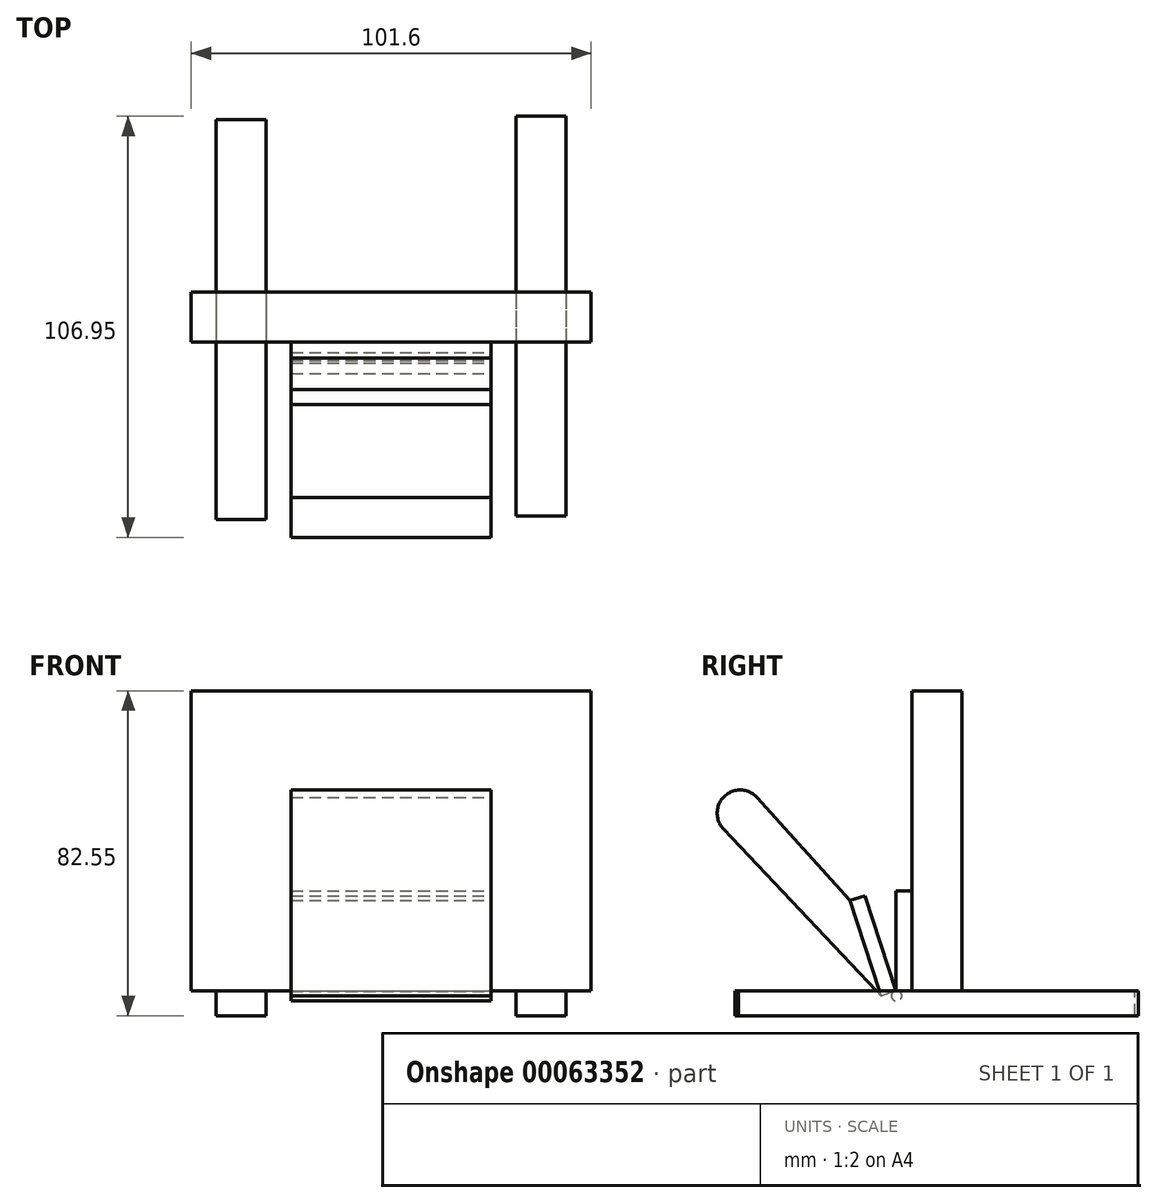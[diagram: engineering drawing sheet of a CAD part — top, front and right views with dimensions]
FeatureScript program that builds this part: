
annotation { "Feature Type Name" : "Feature", "Feature Type Description" : "" }
export const myFeature = defineFeature(function(context is Context, id is Id, definition is map)
    precondition{}
    {
        {
            var Q0;
            Q0=qCreatedBy(makeId("Front.planeOp"),FACE);
            var sketch = newSketch(context, id + "F0", { "sketchPlane" : qUnion([Q0])});
            skLineSegment(sketch, "E0.bottom", {"start": v(0, 0) * mm, "end": v(101.6, 0) * mm});
            skLineSegment(sketch, "E0.top", {"start": v(0, 76.2) * mm, "end": v(101.6, 76.2) * mm});
            skLineSegment(sketch, "E0.left", {"start": v(0, 0) * mm, "end": v(0, 76.2) * mm});
            skLineSegment(sketch, "E0.right", {"start": v(101.6, 0) * mm, "end": v(101.6, 76.2) * mm});
            skSolve(sketch);
        }
        {
            var Q0;
            Q0 = qSketchRegion(id + "F0", true);
            extrude(context, id + "F1", {"entities" : qUnion([Q0]), "depth" : 12.7 * mm});
        }
        {
            var Q0;
            Q0=makeQuery(id+"F1.opExtrude","CAP_FACE",FACE,{"disambiguationData":[OSD([sQuery(id+"F0.wireOp",EDGE,"E0.bottom"),sQuery(id+"F0.wireOp",EDGE,"E0.top"),sQuery(id+"F0.wireOp",EDGE,"E0.left"),sQuery(id+"F0.wireOp",EDGE,"E0.right")])],"isStart":false});
            var sketch = newSketch(context, id + "F2", { "sketchPlane" : qUnion([Q0])});
            skLineSegment(sketch, "E1.rect.bottom", {"start": v(25.4, 0) * mm, "end": v(76.2, 0) * mm});
            skLineSegment(sketch, "E1.rect.top", {"start": v(25.4, 25.4) * mm, "end": v(76.2, 25.4) * mm});
            skLineSegment(sketch, "E1.rect.left", {"start": v(25.4, 0) * mm, "end": v(25.4, 25.4) * mm});
            skLineSegment(sketch, "E1.rect.right", {"start": v(76.2, 0) * mm, "end": v(76.2, 25.4) * mm});
            skPoint(sketch, "E1.rect.middle", {"position": v(50.8, 12.7) * mm});
            skPoint(sketch, "E1.rect.middle.positionSnap0", {"position": v(50.8, 0) * mm});
            skPoint(sketch, "E1.rect.centerSnap0", {"position": v(50.8, 0) * mm});
            skSolve(sketch);
        }
        {
            var Q0;
            Q0 = qSketchRegion(id + "F2", true);
            extrude(context, id + "F3", {"entities" : qUnion([Q0]), "operationType" : NewBodyOperationType.ADD, "depth" : 4.06 * mm});
        }
        {
            var Q0;
            Q0=makeQuery(id+"F3.opExtrude","SWEPT_FACE",FACE,{"disambiguationData":[OSD([sQuery(id+"F2.wireOp",EDGE,"E1.rect.right")])]});
            var sketch = newSketch(context, id + "F4", { "sketchPlane" : qUnion([Q0])});
            skLineSegment(sketch, "E2", {"start": v(-16.76, 0) * mm, "end": v(-24.66, 24.14) * mm});
            skLineSegment(sketch, "E3", {"start": v(-24.66, 24.14) * mm, "end": v(-28.52, 22.88) * mm});
            skLineSegment(sketch, "E4", {"start": v(-28.52, 22.88) * mm, "end": v(-20.63, -1.26) * mm});
            skLineSegment(sketch, "E5", {"start": v(-20.63, -1.26) * mm, "end": v(-16.76, 0) * mm});
            skSolve(sketch);
        }
        {
            var Q0;
            Q0=makeQuery(id+"F4.imprint","IMPRINT",FACE,{"disambiguationData":[TD([[makeQuery(id+"F4.imprint","IMPRINT",EDGE,{"derivedFrom":sQuery(id+"F4.wireOp",EDGE,"E2")}),1.0]])]});
            extrude(context, id + "F5", {"entities" : qUnion([Q0]), "oppositeDirection" : true, "depth" : 50.8 * mm});
        }
        {
            var Q0;
            Q0=makeQuery(id+"F3.opExtrude","SWEPT_FACE",FACE,{"disambiguationData":[OSD([sQuery(id+"F2.wireOp",EDGE,"E1.rect.right")])]});
            var sketch = newSketch(context, id + "F6", { "sketchPlane" : qUnion([Q0])});
            skCircle(sketch, "E6", {"center": v(-16.66, -1.31) * mm, "radius": 1.32 * mm});
            skPoint(sketch, "E6.first.point", {"position": v(-16.76, 0) * mm});
            skPoint(sketch, "E6.second.point", {"position": v(-16.34, -2.6) * mm});
            skPoint(sketch, "E6.third.point", {"position": v(-16.76, -2.63) * mm});
            skSolve(sketch);
        }
        {
            var Q0;
            {var subQ0=sQuery(id+"F6.wireOp",EDGE,"E6");var subQ1=sQuery(id+"F2.wireOp",EDGE,"E1.rect.right");var subQ2=makeQuery(id+"F3.opExtrude","SWEPT_EDGE",EDGE,{"disambiguationData":[OSD([sQuery(id+"F0.wireOp",EDGE,"E0.bottom"),sQuery(id+"F2.wireOp",EDGE,"E1.rect.bottom"),subQ1])]});var subQ4=makeQuery(id+"F6.imprint","INTERSECT",VERTEX,{"derivedFrom":[subQ2,subQ0]});Q0=makeQuery(id+"F6.imprint","IMPRINT",FACE,{"disambiguationData":[TD([[makeQuery(id+"F6.imprint","IMPRINT",EDGE,{"disambiguationData":[TD([[subQ4,1.0]])],"derivedFrom":subQ0}),1.0]])]});}
            extrude(context, id + "F7", {"entities" : qUnion([Q0]), "operationType" : NewBodyOperationType.ADD, "oppositeDirection" : true, "depth" : 50.8 * mm});
        }
        {
            var Q0;
            Q0=makeQuery(id+"F7.boolean.opBoolean","MERGE",FACE,{"derivedFrom":[makeQuery(id+"F5.opExtrude","CAP_FACE",FACE,{"disambiguationData":[OSD([sQuery(id+"F4.wireOp",EDGE,"E2"),sQuery(id+"F4.wireOp",EDGE,"E3"),sQuery(id+"F4.wireOp",EDGE,"E4"),sQuery(id+"F4.wireOp",EDGE,"E5")])],"isStart":true}),makeQuery(id+"F7.opExtrude","CAP_FACE",FACE,{"disambiguationData":[OSD([sQuery(id+"F0.wireOp",EDGE,"E0.bottom"),sQuery(id+"F2.wireOp",EDGE,"E1.rect.bottom"),sQuery(id+"F2.wireOp",EDGE,"E1.rect.right"),sQuery(id+"F6.wireOp",EDGE,"E6")])],"isStart":true})]});
            var sketch = newSketch(context, id + "F8", { "sketchPlane" : qUnion([Q0])});
            skLineSegment(sketch, "E7", {"start": v(-28.52, 22.88) * mm, "end": v(-52.1, 49.1) * mm});
            skLineSegment(sketch, "E8", {"start": v(-20.63, -1.26) * mm, "end": v(-60.64, 41.1) * mm});
            skArc(sketch, "E9", {"start": v(-52.1, 49.1) * mm, "mid": v(-60.4, 49.38) * mm, "end": v(-60.64, 41.1) * mm});
            skSolve(sketch);
        }
        {
            var Q0;
            Q0=makeQuery(id+"F8.imprint","IMPRINT",FACE,{"disambiguationData":[TD([[makeQuery(id+"F8.imprint","IMPRINT",EDGE,{"derivedFrom":sQuery(id+"F8.wireOp",EDGE,"E7")}),1.0]])]});
            extrude(context, id + "F9", {"entities" : qUnion([Q0]), "oppositeDirection" : true, "depth" : 50.8 * mm});
        }
        {
            var Q0;
            Q0=makeQuery(id+"F3.boolean.opBoolean","MERGE",FACE,{"derivedFrom":[makeQuery(id+"F1.opExtrude","SWEPT_FACE",FACE,{"disambiguationData":[OSD([sQuery(id+"F0.wireOp",EDGE,"E0.bottom")])]}),makeQuery(id+"F3.opExtrude","SWEPT_FACE",FACE,{"disambiguationData":[OSD([sQuery(id+"F2.wireOp",EDGE,"E1.rect.bottom")])]})]});
            var sketch = newSketch(context, id + "F10", { "sketchPlane" : qUnion([Q0])});
            skLineSegment(sketch, "E10.rect.bottom", {"start": v(95.25, -44.71) * mm, "end": v(82.55, -44.71) * mm});
            skLineSegment(sketch, "E10.rect.top", {"start": v(95.25, 56.89) * mm, "end": v(82.55, 56.89) * mm});
            skLineSegment(sketch, "E10.rect.left", {"start": v(95.25, -44.71) * mm, "end": v(95.25, 56.89) * mm});
            skLineSegment(sketch, "E10.rect.right", {"start": v(82.55, -44.71) * mm, "end": v(82.55, 56.89) * mm});
            skPoint(sketch, "E10.rect.middle", {"position": v(88.9, 6.09) * mm});
            skPoint(sketch, "E10.rect.middle.positionSnap0", {"position": v(88.9, 12.7) * mm});
            skPoint(sketch, "E10.rect.centerSnap0", {"position": v(88.9, 12.7) * mm});
            skSolve(sketch);
        }
        {
            var Q0;
            Q0 = qSketchRegion(id + "F10", true);
            extrude(context, id + "F11", {"entities" : qUnion([Q0]), "operationType" : NewBodyOperationType.ADD, "depth" : 6.35 * mm});
        }
        {
            var Q0;
            {var subQ0=sQuery(id+"F0.wireOp",EDGE,"E0.left");var subQ3=sQuery(id+"F0.wireOp",EDGE,"E0.bottom");var subQ6=sQuery(id+"F2.wireOp",EDGE,"E1.rect.bottom");Q0=makeQuery(id+"F11.boolean.opBoolean","SPLIT",FACE,{"disambiguationData":[TD([makeQuery(id+"F1.opExtrude","SWEPT_FACE",FACE,{"disambiguationData":[OSD([subQ0])]})])],"derivedFrom":makeQuery(id+"F3.boolean.opBoolean","MERGE",FACE,{"derivedFrom":[makeQuery(id+"F1.opExtrude","SWEPT_FACE",FACE,{"disambiguationData":[OSD([subQ3])]}),makeQuery(id+"F3.opExtrude","SWEPT_FACE",FACE,{"disambiguationData":[OSD([subQ6])]})]})});}
            var sketch = newSketch(context, id + "F12", { "sketchPlane" : qUnion([Q0])});
            skLineSegment(sketch, "E11.rect.bottom", {"start": v(19.05, -43.9) * mm, "end": v(6.35, -43.9) * mm});
            skLineSegment(sketch, "E11.rect.top", {"start": v(19.05, 57.7) * mm, "end": v(6.35, 57.7) * mm});
            skLineSegment(sketch, "E11.rect.left", {"start": v(19.05, -43.9) * mm, "end": v(19.05, 57.7) * mm});
            skLineSegment(sketch, "E11.rect.right", {"start": v(6.35, -43.9) * mm, "end": v(6.35, 57.7) * mm});
            skPoint(sketch, "E11.rect.middle", {"position": v(12.7, 6.9) * mm});
            skPoint(sketch, "E11.rect.middle.positionSnap0", {"position": v(12.7, 12.7) * mm});
            skPoint(sketch, "E11.rect.centerSnap0", {"position": v(12.7, 12.7) * mm});
            skSolve(sketch);
        }
        {
            var Q0;
            Q0 = qSketchRegion(id + "F12", true);
            extrude(context, id + "F13", {"entities" : qUnion([Q0]), "operationType" : NewBodyOperationType.ADD, "depth" : 6.35 * mm});
        }
    });
